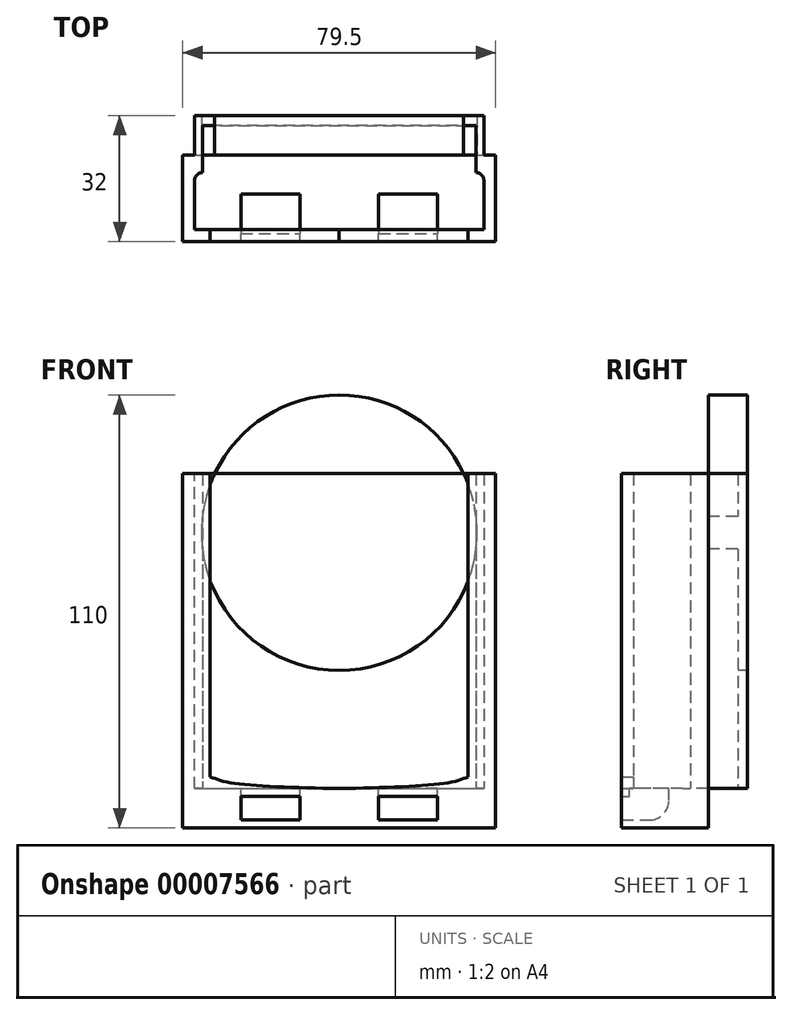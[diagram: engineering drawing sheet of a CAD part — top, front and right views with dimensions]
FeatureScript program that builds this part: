
annotation { "Feature Type Name" : "Feature", "Feature Type Description" : "" }
export const myFeature = defineFeature(function(context is Context, id is Id, definition is map)
    precondition{}
    {
        {
            var Q0;
            Q0=qCreatedBy(makeId("Top.planeOp"),FACE);
            var sketch = newSketch(context, id + "F0", { "sketchPlane" : qUnion([Q0])});
            skLineSegment(sketch, "E0.bottom", {"start": v(-35.13, 7.4) * mm, "end": v(38.37, 7.4) * mm});
            skLineSegment(sketch, "E0.top", {"start": v(-35.13, -7.1) * mm, "end": v(38.37, -7.1) * mm});
            skLineSegment(sketch, "E0.left", {"start": v(-35.13, 7.4) * mm, "end": v(-35.13, -7.1) * mm});
            skLineSegment(sketch, "E0.right", {"start": v(38.37, 7.4) * mm, "end": v(38.37, -7.1) * mm});
            skLineSegment(sketch, "E1", {"start": v(1.62, 16.77) * mm, "end": v(1.62, -7.1) * mm, "construction": true});
            skLineSegment(sketch, "E2", {"start": v(-35.13, 0.15) * mm, "end": v(38.37, 0.15) * mm, "construction": true});
            skLineSegment(sketch, "E3", {"start": v(-31.13, -7.1) * mm, "end": v(-31.13, -10.1) * mm});
            skLineSegment(sketch, "E4", {"start": v(-31.13, -10.1) * mm, "end": v(-38.13, -10.1) * mm});
            skLineSegment(sketch, "E5", {"start": v(-38.13, -10.1) * mm, "end": v(-38.13, 11.9) * mm});
            skPoint(sketch, "E6.orphan", {"position": v(1.62, 7.4) * mm});
            skLineSegment(sketch, "E7", {"start": v(-38.13, 11.9) * mm, "end": v(1.62, 11.9) * mm});
            skLineSegment(sketch, "E8", {"start": v(1.62, 7.4) * mm, "end": v(1.62, 11.9) * mm});
            skLineSegment(sketch, "E9.0.MirrorCS", {"start": v(41.37, 11.9) * mm, "end": v(1.62, 11.9) * mm});
            skLineSegment(sketch, "E10.0.MirrorCS", {"start": v(41.37, -10.1) * mm, "end": v(41.37, 11.9) * mm});
            skLineSegment(sketch, "E11.0.MirrorCS", {"start": v(34.37, -10.1) * mm, "end": v(41.37, -10.1) * mm});
            skLineSegment(sketch, "E12.0.MirrorCS", {"start": v(34.37, -7.1) * mm, "end": v(34.37, -10.1) * mm});
            skSolve(sketch);
        }
        {
            var Q0;
            {var subQ1=sQuery(id+"F0.wireOp",EDGE,"E0.left");Q0=makeQuery(id+"F0.imprint","IMPRINT",FACE,{"disambiguationData":[TD([[makeQuery(id+"F0.imprint","IMPRINT",EDGE,{"derivedFrom":subQ1}),-1.0]])]});}
            var Q1;
            {var subQ2=sQuery(id+"F0.wireOp",EDGE,"E0.right");Q1=makeQuery(id+"F0.imprint","IMPRINT",FACE,{"disambiguationData":[TD([[makeQuery(id+"F0.imprint","IMPRINT",EDGE,{"derivedFrom":subQ2}),1.0]])]});}
            extrude(context, id + "F1", {"entities" : qUnion([Q0, Q1]), "depth" : 80 * mm});
        }
        {
            var Q0;
            Q0=makeQuery(id+"F1.opExtrude","SWEPT_EDGE",EDGE,{"disambiguationData":[OSD([sQuery(id+"F0.wireOp",EDGE,"E0.bottom"),sQuery(id+"F0.wireOp",EDGE,"E0.left")])]});
            var Q1;
            Q1=makeQuery(id+"F1.opExtrude","SWEPT_EDGE",EDGE,{"disambiguationData":[OSD([sQuery(id+"F0.wireOp",EDGE,"E0.bottom"),sQuery(id+"F0.wireOp",EDGE,"E0.right")])]});
            fillet(context, id + "F2", {"entities" : qUnion([Q0, Q1]), "radius" : 2 * mm, "tangentPropagation" : true, "allowEdgeOverflow" : false});
        }
        {
            var Q0;
            {var subQ1=sQuery(id+"F0.wireOp",EDGE,"E0.left");Q0=makeQuery(id+"F0.imprint","IMPRINT",FACE,{"disambiguationData":[TD([[makeQuery(id+"F0.imprint","IMPRINT",EDGE,{"derivedFrom":subQ1}),1.0]])]});}
            var Q1;
            {var subQ1=sQuery(id+"F0.wireOp",EDGE,"E0.left");Q1=makeQuery(id+"F0.imprint","IMPRINT",FACE,{"disambiguationData":[TD([[makeQuery(id+"F0.imprint","IMPRINT",EDGE,{"derivedFrom":subQ1}),-1.0]])]});}
            var Q2;
            {var subQ2=sQuery(id+"F0.wireOp",EDGE,"E0.right");Q2=makeQuery(id+"F0.imprint","IMPRINT",FACE,{"disambiguationData":[TD([[makeQuery(id+"F0.imprint","IMPRINT",EDGE,{"derivedFrom":subQ2}),1.0]])]});}
            extrude(context, id + "F3", {"entities" : qUnion([Q0, Q1, Q2]), "operationType" : NewBodyOperationType.ADD, "oppositeDirection" : true, "depth" : 10 * mm});
        }
        {
            var Q0;
            Q0=makeQuery(id+"F3.opExtrude","SWEPT_FACE",FACE,{"disambiguationData":[OSD([sQuery(id+"F0.wireOp",EDGE,"E0.top")])]});
            var sketch = newSketch(context, id + "F4", { "sketchPlane" : qUnion([Q0])});
            skLineSegment(sketch, "E13.bottom", {"start": v(-23.38, -2) * mm, "end": v(-8.38, -2) * mm});
            skLineSegment(sketch, "E13.top", {"start": v(-23.38, -8) * mm, "end": v(-8.38, -8) * mm});
            skLineSegment(sketch, "E13.left", {"start": v(-23.38, -2) * mm, "end": v(-23.38, -8) * mm});
            skLineSegment(sketch, "E13.right", {"start": v(-8.38, -2) * mm, "end": v(-8.38, -8) * mm});
            skLineSegment(sketch, "E14", {"start": v(-15.88, -8) * mm, "end": v(-15.88, -10) * mm, "construction": true});
            skLineSegment(sketch, "E15", {"start": v(-15.88, -2) * mm, "end": v(-15.88, 0) * mm, "construction": true});
            skLineSegment(sketch, "E16", {"start": v(-31.13, 0) * mm, "end": v(-31.13, 3) * mm});
            skLineSegment(sketch, "E17", {"start": v(1.62, -10) * mm, "end": v(1.62, 0) * mm, "construction": true});
            skFitSpline(sketch, "E18", {"points": [v(-31.13, 3) * mm, v(-26.06, 1.48) * mm, v(1.62, 0) * mm], "startDerivative": vector(13.16, -5.42) * mm, "endDerivative": vector(47.81, -1.14) * mm});
            skLineSegment(sketch, "E19", {"start": v(-31.13, 0) * mm, "end": v(1.62, 0) * mm});
            skLineSegment(sketch, "E20.0.MirrorCS", {"start": v(11.62, -2) * mm, "end": v(11.62, -8) * mm});
            skLineSegment(sketch, "E21.0.MirrorCS", {"start": v(26.62, -8) * mm, "end": v(11.62, -8) * mm});
            skLineSegment(sketch, "E22.0.MirrorCS", {"start": v(26.62, -2) * mm, "end": v(26.62, -8) * mm});
            skLineSegment(sketch, "E23.0.MirrorCS", {"start": v(26.62, -2) * mm, "end": v(11.62, -2) * mm});
            skFitSpline(sketch, "E24.0.MirrorCS", {"points": [v(34.37, 3) * mm, v(29.3, 1.48) * mm, v(1.62, 0) * mm], "startDerivative": vector(-13.16, -5.42) * mm, "endDerivative": vector(-47.81, -1.14) * mm});
            skLineSegment(sketch, "E25.0.MirrorCS", {"start": v(34.37, 0) * mm, "end": v(34.37, 3) * mm});
            skSolve(sketch);
        }
        {
            var Q0;
            Q0=makeQuery(id+"F4.imprint","IMPRINT",FACE,{"disambiguationData":[TD([[makeQuery(id+"F4.imprint","IMPRINT",EDGE,{"derivedFrom":sQuery(id+"F4.wireOp",EDGE,"E13.bottom")}),1.0]])]});
            extrude(context, id + "F5", {"entities" : qUnion([Q0]), "operationType" : NewBodyOperationType.ADD, "depth" : 3 * mm});
        }
        {
            var Q0;
            {var subQ0=sQuery(id+"F0.wireOp",EDGE,"E0.top");Q0=makeQuery(id+"F5.boolean.opBoolean","MERGE",FACE,{"derivedFrom":[makeQuery(id+"F3.opExtrude","CAP_FACE",FACE,{"disambiguationData":[OSD([subQ0,sQuery(id+"F0.wireOp",EDGE,"E3"),sQuery(id+"F0.wireOp",EDGE,"E4"),sQuery(id+"F0.wireOp",EDGE,"E5"),sQuery(id+"F0.wireOp",EDGE,"E7"),sQuery(id+"F0.wireOp",EDGE,"E9.0.MirrorCS"),sQuery(id+"F0.wireOp",EDGE,"E10.0.MirrorCS"),sQuery(id+"F0.wireOp",EDGE,"E11.0.MirrorCS"),sQuery(id+"F0.wireOp",EDGE,"E12.0.MirrorCS")])],"isStart":true}),makeQuery(id+"F5.opExtrude","SWEPT_FACE",FACE,{"disambiguationData":[OSD([subQ0,sQuery(id+"F4.wireOp",EDGE,"E19")])]})]});}
            var sketch = newSketch(context, id + "F6", { "sketchPlane" : qUnion([Q0])});
            skLineSegment(sketch, "E26.bottom", {"start": v(-23.38, 1.9) * mm, "end": v(-8.38, 1.9) * mm});
            skLineSegment(sketch, "E26.top", {"start": v(-23.38, -8.1) * mm, "end": v(-8.38, -8.1) * mm});
            skLineSegment(sketch, "E26.left", {"start": v(-23.38, 1.9) * mm, "end": v(-23.38, -8.1) * mm});
            skLineSegment(sketch, "E26.right", {"start": v(-8.38, 1.9) * mm, "end": v(-8.38, -8.1) * mm});
            skLineSegment(sketch, "E27", {"start": v(1.62, 7.4) * mm, "end": v(1.62, -10.1) * mm, "construction": true});
            skLineSegment(sketch, "E28.0.MirrorCS", {"start": v(11.62, 1.9) * mm, "end": v(11.62, -8.1) * mm});
            skLineSegment(sketch, "E29.0.MirrorCS", {"start": v(26.62, -8.1) * mm, "end": v(11.62, -8.1) * mm});
            skLineSegment(sketch, "E30.0.MirrorCS", {"start": v(26.62, 1.9) * mm, "end": v(26.62, -8.1) * mm});
            skLineSegment(sketch, "E31.0.MirrorCS", {"start": v(26.62, 1.9) * mm, "end": v(11.62, 1.9) * mm});
            skSolve(sketch);
        }
        {
            var Q0;
            Q0=makeQuery(id+"F6.imprint","IMPRINT",FACE,{"disambiguationData":[TD([[makeQuery(id+"F6.imprint","IMPRINT",EDGE,{"derivedFrom":sQuery(id+"F6.wireOp",EDGE,"E26.bottom")}),-1.0]])]});
            var Q1;
            Q1=makeQuery(id+"F6.imprint","IMPRINT",FACE,{"disambiguationData":[TD([[makeQuery(id+"F6.imprint","IMPRINT",EDGE,{"derivedFrom":sQuery(id+"F6.wireOp",EDGE,"E28.0.MirrorCS")}),1.0]])]});
            var Q2;
            Q2=makeQuery(id+"F5.opExtrude","SWEPT_FACE",FACE,{"disambiguationData":[OSD([sQuery(id+"F4.wireOp",EDGE,"E13.top")])]});
            extrude(context, id + "F7", {"entities" : qUnion([Q0, Q1]), "operationType" : NewBodyOperationType.REMOVE, "endBound" : BoundingType.UP_TO_SURFACE, "oppositeDirection" : true, "endBoundEntityFace" : qUnion([Q2]), "depth" : 8.12 * mm});
        }
        {
            var Q0;
            Q0=makeQuery(id+"F4.imprint","IMPRINT",FACE,{"disambiguationData":[TD([[makeQuery(id+"F4.imprint","IMPRINT",EDGE,{"derivedFrom":sQuery(id+"F4.wireOp",EDGE,"E13.bottom")}),-1.0]])]});
            var Q1;
            Q1=makeQuery(id+"F4.imprint","IMPRINT",FACE,{"disambiguationData":[TD([[makeQuery(id+"F4.imprint","IMPRINT",EDGE,{"derivedFrom":sQuery(id+"F4.wireOp",EDGE,"E20.0.MirrorCS")}),1.0]])]});
            var Q2;
            Q2=makeQuery(id+"F7.boolean.opBoolean","COPY",FACE,{"derivedFrom":makeQuery(id+"F7.opExtrude","SWEPT_FACE",FACE,{"disambiguationData":[OSD([sQuery(id+"F6.wireOp",EDGE,"E26.bottom")])]})});
            extrude(context, id + "F8", {"entities" : qUnion([Q0, Q1]), "operationType" : NewBodyOperationType.REMOVE, "endBound" : BoundingType.UP_TO_SURFACE, "oppositeDirection" : true, "endBoundEntityFace" : qUnion([Q2]), "depth" : 7.57 * mm});
        }
        {
            var Q0;
            Q0=makeQuery(id+"F7.boolean.opBoolean","COPY",EDGE,{"derivedFrom":makeQuery(id+"F7.opExtrude","CAP_EDGE",EDGE,{"disambiguationData":[OSD([sQuery(id+"F6.wireOp",EDGE,"E26.bottom")])],"isStart":false})});
            var Q1;
            Q1=makeQuery(id+"F7.boolean.opBoolean","COPY",EDGE,{"derivedFrom":makeQuery(id+"F7.opExtrude","CAP_EDGE",EDGE,{"disambiguationData":[OSD([sQuery(id+"F6.wireOp",EDGE,"E31.0.MirrorCS")])],"isStart":false})});
            fillet(context, id + "F9", {"entities" : qUnion([Q0, Q1]), "radius" : 5 * mm, "tangentPropagation" : true, "allowEdgeOverflow" : false});
        }
        {
            var Q0;
            Q0=makeQuery(id+"F4.imprint","IMPRINT",FACE,{"disambiguationData":[TD([[makeQuery(id+"F4.imprint","IMPRINT",EDGE,{"derivedFrom":sQuery(id+"F4.wireOp",EDGE,"E16")}),-1.0]])]});
            var Q1;
            {var subQ2=sQuery(id+"F4.wireOp",EDGE,"E24.0.MirrorCS");Q1=makeQuery(id+"F4.imprint","IMPRINT",FACE,{"disambiguationData":[TD([[makeQuery(id+"F4.imprint","IMPRINT",EDGE,{"derivedFrom":subQ2}),1.0]])]});}
            var Q2;
            Q2=makeQuery(id+"F7.boolean.opBoolean","COPY",FACE,{"derivedFrom":makeQuery(id+"F7.opExtrude","SWEPT_FACE",FACE,{"disambiguationData":[OSD([sQuery(id+"F6.wireOp",EDGE,"E29.0.MirrorCS")])]})});
            var Q3;
            {var subQ0=sQuery(id+"F0.wireOp",EDGE,"E4");var subQ1=sQuery(id+"F0.wireOp",EDGE,"E11.0.MirrorCS");Q3=makeQuery(id+"F5.boolean.opBoolean","MERGE",FACE,{"derivedFrom":[makeQuery(id+"F3.boolean.opBoolean","MERGE",FACE,{"derivedFrom":[makeQuery(id+"F1.opExtrude","SWEPT_FACE",FACE,{"disambiguationData":[OSD([subQ0])]}),makeQuery(id+"F3.opExtrude","SWEPT_FACE",FACE,{"disambiguationData":[OSD([subQ0])]})]}),makeQuery(id+"F3.boolean.opBoolean","MERGE",FACE,{"derivedFrom":[makeQuery(id+"F1.opExtrude","SWEPT_FACE",FACE,{"disambiguationData":[OSD([subQ1])]}),makeQuery(id+"F3.opExtrude","SWEPT_FACE",FACE,{"disambiguationData":[OSD([subQ1])]})]}),makeQuery(id+"F5.opExtrude","CAP_FACE",FACE,{"disambiguationData":[OSD([sQuery(id+"F0.wireOp",EDGE,"E0.top"),sQuery(id+"F0.wireOp",EDGE,"E3"),sQuery(id+"F0.wireOp",EDGE,"E12.0.MirrorCS"),sQuery(id+"F4.wireOp",EDGE,"E13.bottom"),sQuery(id+"F4.wireOp",EDGE,"E13.top"),sQuery(id+"F4.wireOp",EDGE,"E13.left"),sQuery(id+"F4.wireOp",EDGE,"E13.right"),sQuery(id+"F4.wireOp",EDGE,"E19"),sQuery(id+"F4.wireOp",EDGE,"E20.0.MirrorCS"),sQuery(id+"F4.wireOp",EDGE,"E21.0.MirrorCS"),sQuery(id+"F4.wireOp",EDGE,"E22.0.MirrorCS"),sQuery(id+"F4.wireOp",EDGE,"E23.0.MirrorCS")])],"isStart":false})]});}
            extrude(context, id + "F10", {"entities" : qUnion([Q0, Q1, Q2]), "operationType" : NewBodyOperationType.ADD, "endBound" : BoundingType.UP_TO_SURFACE, "endBoundEntityFace" : qUnion([Q3]), "depth" : 25 * mm});
        }
        {
            var Q0;
            {var subQ0=sQuery(id+"F0.wireOp",EDGE,"E7");var subQ1=sQuery(id+"F0.wireOp",EDGE,"E9.0.MirrorCS");Q0=makeQuery(id+"F3.boolean.opBoolean","MERGE",FACE,{"derivedFrom":[makeQuery(id+"F1.opExtrude","SWEPT_FACE",FACE,{"disambiguationData":[OSD([subQ0,subQ1])]}),makeQuery(id+"F3.opExtrude","SWEPT_FACE",FACE,{"disambiguationData":[OSD([subQ0,subQ1])]})]});}
            var sketch = newSketch(context, id + "F11", { "sketchPlane" : qUnion([Q0])});
            skCircle(sketch, "E32", {"center": v(-1.62, 65) * mm, "radius": 35 * mm});
            skLineSegment(sketch, "E33", {"start": v(-1.62, 80) * mm, "end": v(-1.62, 93.64) * mm, "construction": true});
            skArc(sketch, "E34.0", {"start": v(35.13, 49.2) * mm, "mid": v(-1.62, 105) * mm, "end": v(-38.37, 49.2) * mm});
            skLineSegment(sketch, "E35.0.1", {"start": v(-38.37, 80) * mm, "end": v(-38.37, 0) * mm});
            skLineSegment(sketch, "E35.0.3", {"start": v(-38.37, 0) * mm, "end": v(-38.37, 80) * mm});
            skLineSegment(sketch, "E35.1.1", {"start": v(35.13, 0) * mm, "end": v(35.13, 80) * mm});
            skLineSegment(sketch, "E35.1.3", {"start": v(35.13, 80) * mm, "end": v(35.13, 0) * mm});
            skLineSegment(sketch, "E36.bottom", {"start": v(35.13, 0) * mm, "end": v(-38.37, 0) * mm});
            skLineSegment(sketch, "E36.top", {"start": v(35.13, 105.47) * mm, "end": v(-38.37, 105.47) * mm, "construction": true});
            skLineSegment(sketch, "E36.left", {"start": v(-38.37, 0) * mm, "end": v(-38.37, 105.47) * mm, "construction": true});
            skLineSegment(sketch, "E36.right", {"start": v(35.13, 0) * mm, "end": v(35.13, 105.47) * mm, "construction": true});
            skArc(sketch, "E37.trimOffspring", {"start": v(-38.37, 80.8) * mm, "mid": v(-1.62, 25) * mm, "end": v(35.13, 80.8) * mm});
            skSolve(sketch);
        }
        {
            var Q0;
            {var subQ2=sQuery(id+"F11.wireOp",EDGE,"E37.trimOffspring");var subQ4=sQuery(id+"F11.wireOp",EDGE,"E35.0.3");var subQ10=makeQuery(id+"F11.imprint","INTERSECT",VERTEX,{"derivedFrom":[subQ4,subQ2]});Q0=makeQuery(id+"F11.imprint","IMPRINT",FACE,{"disambiguationData":[TD([[makeQuery(id+"F11.imprint","IMPRINT",EDGE,{"disambiguationData":[TD([[subQ10,-1.0]])],"derivedFrom":subQ4}),1.0]])]});}
            var Q1;
            {var subQ6=sQuery(id+"F11.wireOp",EDGE,"E35.0.3");var subQ8=sQuery(id+"F11.wireOp",EDGE,"E37.trimOffspring");var subQ10=makeQuery(id+"F11.imprint","INTERSECT",VERTEX,{"derivedFrom":[subQ6,subQ8]});Q1=makeQuery(id+"F11.imprint","IMPRINT",FACE,{"disambiguationData":[TD([[makeQuery(id+"F11.imprint","IMPRINT",EDGE,{"disambiguationData":[TD([[subQ10,-1.0]])],"derivedFrom":subQ8}),1.0]])]});}
            var Q2;
            Q2=makeQuery(id+"F11.imprint","IMPRINT",FACE,{"disambiguationData":[TD([[makeQuery(id+"F11.imprint","IMPRINT",EDGE,{"derivedFrom":sQuery(id+"F11.wireOp",EDGE,"c73c8027-a30e-4751-a17e-f7e3be50884d")}),-1.0]])]});
            var Q3;
            {var subQ1=sQuery(id+"F0.wireOp",EDGE,"E7");var subQ3=sQuery(id+"F11.wireOp",EDGE,"E37.trimOffspring");var subQ5=makeQuery(id+"F1.opExtrude","CAP_EDGE",EDGE,{"disambiguationData":[OSD([subQ1,sQuery(id+"F0.wireOp",EDGE,"E9.0.MirrorCS")])],"isStart":false});var subQ7=makeQuery(id+"F11.imprint","INTERSECT",VERTEX,{"disambiguationData":[OD(1.0)],"derivedFrom":[subQ5,subQ3]});Q3=makeQuery(id+"F11.imprint","IMPRINT",FACE,{"disambiguationData":[TD([[makeQuery(id+"F11.imprint","IMPRINT",EDGE,{"disambiguationData":[TD([[subQ7,1.0]])],"derivedFrom":subQ3}),-1.0]])]});}
            var Q4;
            {var subQ2=sQuery(id+"F11.wireOp",EDGE,"E37.trimOffspring");var subQ4=sQuery(id+"F11.wireOp",EDGE,"E35.1.3");var subQ10=makeQuery(id+"F11.imprint","INTERSECT",VERTEX,{"derivedFrom":[subQ4,subQ2]});Q4=makeQuery(id+"F11.imprint","IMPRINT",FACE,{"disambiguationData":[TD([[makeQuery(id+"F11.imprint","IMPRINT",EDGE,{"disambiguationData":[TD([[subQ10,1.0]])],"derivedFrom":subQ4}),1.0]])]});}
            var Q5;
            {var subQ0=sQuery(id+"F0.wireOp",EDGE,"E9.0.MirrorCS");var subQ3=sQuery(id+"F11.wireOp",EDGE,"E37.trimOffspring");var subQ5=makeQuery(id+"F1.opExtrude","CAP_EDGE",EDGE,{"disambiguationData":[OSD([sQuery(id+"F0.wireOp",EDGE,"E7"),subQ0])],"isStart":false});var subQ7=makeQuery(id+"F11.imprint","INTERSECT",VERTEX,{"disambiguationData":[OD(0.0)],"derivedFrom":[subQ5,subQ3]});Q5=makeQuery(id+"F11.imprint","IMPRINT",FACE,{"disambiguationData":[TD([[makeQuery(id+"F11.imprint","IMPRINT",EDGE,{"disambiguationData":[TD([[subQ7,-1.0]])],"derivedFrom":subQ3}),-1.0]])]});}
            var Q6;
            {var subQ0=makeQuery(id+"F1.opExtrude","CAP_EDGE",EDGE,{"disambiguationData":[OSD([sQuery(id+"F0.wireOp",EDGE,"E7"),sQuery(id+"F0.wireOp",EDGE,"E9.0.MirrorCS")])],"isStart":false});var subQ1=sQuery(id+"F11.wireOp",EDGE,"E32");var subQ3=makeQuery(id+"F11.imprint","INTERSECT",VERTEX,{"disambiguationData":[OD(0.0)],"derivedFrom":[subQ0,subQ1]});Q6=makeQuery(id+"F11.imprint","IMPRINT",FACE,{"disambiguationData":[TD([[makeQuery(id+"F11.imprint","IMPRINT",EDGE,{"disambiguationData":[TD([[subQ3,-1.0]])],"derivedFrom":subQ1}),1.0]])]});}
            extrude(context, id + "F12", {"entities" : qUnion([Q0, Q1, Q2, Q3, Q4, Q5, Q6]), "operationType" : NewBodyOperationType.ADD, "depth" : 10 * mm});
        }
        {
            var Q0;
            Q0=makeQuery(id+"F1.opExtrude","SWEPT_FACE",FACE,{"disambiguationData":[OSD([sQuery(id+"F0.wireOp",EDGE,"E0.bottom")])]});
            var sketch = newSketch(context, id + "F13", { "sketchPlane" : qUnion([Q0])});
            skCircle(sketch, "E38.0", {"center": v(1.62, 65) * mm, "radius": 35 * mm});
            skCircle(sketch, "E39.0", {"center": v(1.62, 68.67) * mm, "radius": 2 * mm});
            skCircle(sketch, "E40.0", {"center": v(1.62, 59.67) * mm, "radius": 3 * mm});
            skCircle(sketch, "E41.0", {"center": v(1.62, 50.67) * mm, "radius": 2 * mm});
            skCircle(sketch, "E42", {"center": v(1.62, 68.67) * mm, "radius": 4 * mm});
            skCircle(sketch, "E43", {"center": v(1.62, 50.67) * mm, "radius": 4 * mm});
            skSolve(sketch);
        }
        {
            var Q0;
            Q0=makeQuery(id+"F13.imprint","IMPRINT",FACE,{"disambiguationData":[TD([[makeQuery(id+"F13.imprint","IMPRINT",EDGE,{"derivedFrom":sQuery(id+"F13.wireOp",EDGE,"E40.0")}),1.0]])]});
            extrude(context, id + "F14", {"entities" : qUnion([Q0]), "operationType" : NewBodyOperationType.REMOVE, "oppositeDirection" : true, "depth" : 10 * mm});
        }
        {
            var Q0;
            Q0=makeQuery(id+"F14.boolean.opBoolean","SPLIT",FACE,{"disambiguationData":[TD([makeQuery(id+"F14.opExtrude","SWEPT_FACE",FACE,{"disambiguationData":[OSD([sQuery(id+"F13.wireOp",EDGE,"E42")])]})])],"derivedFrom":makeQuery(id+"F1.opExtrude","SWEPT_FACE",FACE,{"disambiguationData":[OSD([sQuery(id+"F0.wireOp",EDGE,"E0.bottom")])]})});
            var Q1;
            Q1=makeQuery(id+"F14.boolean.opBoolean","SPLIT",FACE,{"disambiguationData":[TD([makeQuery(id+"F14.opExtrude","SWEPT_FACE",FACE,{"disambiguationData":[OSD([sQuery(id+"F13.wireOp",EDGE,"E40.0")])]})])],"derivedFrom":makeQuery(id+"F1.opExtrude","SWEPT_FACE",FACE,{"disambiguationData":[OSD([sQuery(id+"F0.wireOp",EDGE,"E0.bottom")])]})});
            var Q2;
            Q2=makeQuery(id+"F14.boolean.opBoolean","SPLIT",FACE,{"disambiguationData":[TD([makeQuery(id+"F14.opExtrude","SWEPT_FACE",FACE,{"disambiguationData":[OSD([sQuery(id+"F13.wireOp",EDGE,"E43")])]})])],"derivedFrom":makeQuery(id+"F1.opExtrude","SWEPT_FACE",FACE,{"disambiguationData":[OSD([sQuery(id+"F0.wireOp",EDGE,"E0.bottom")])]})});
            extrude(context, id + "F15", {"entities" : qUnion([Q0, Q1, Q2]), "operationType" : NewBodyOperationType.REMOVE, "oppositeDirection" : true, "depth" : 12 * mm});
        }
        {
            var Q0;
            Q0=makeQuery(id+"F13.imprint","IMPRINT",FACE,{"disambiguationData":[TD([[makeQuery(id+"F13.imprint","IMPRINT",EDGE,{"derivedFrom":sQuery(id+"F13.wireOp",EDGE,"E39.0")}),-1.0]])]});
            var Q1;
            Q1=makeQuery(id+"F13.imprint","IMPRINT",FACE,{"disambiguationData":[TD([[makeQuery(id+"F13.imprint","IMPRINT",EDGE,{"derivedFrom":sQuery(id+"F13.wireOp",EDGE,"E40.0")}),-1.0]])]});
            var Q2;
            Q2=makeQuery(id+"F13.imprint","IMPRINT",FACE,{"disambiguationData":[TD([[makeQuery(id+"F13.imprint","IMPRINT",EDGE,{"derivedFrom":sQuery(id+"F13.wireOp",EDGE,"E41.0")}),-1.0]])]});
            extrude(context, id + "F16", {"entities" : qUnion([Q0, Q1, Q2]), "operationType" : NewBodyOperationType.REMOVE, "oppositeDirection" : true, "depth" : 25 * mm});
        }
    });
